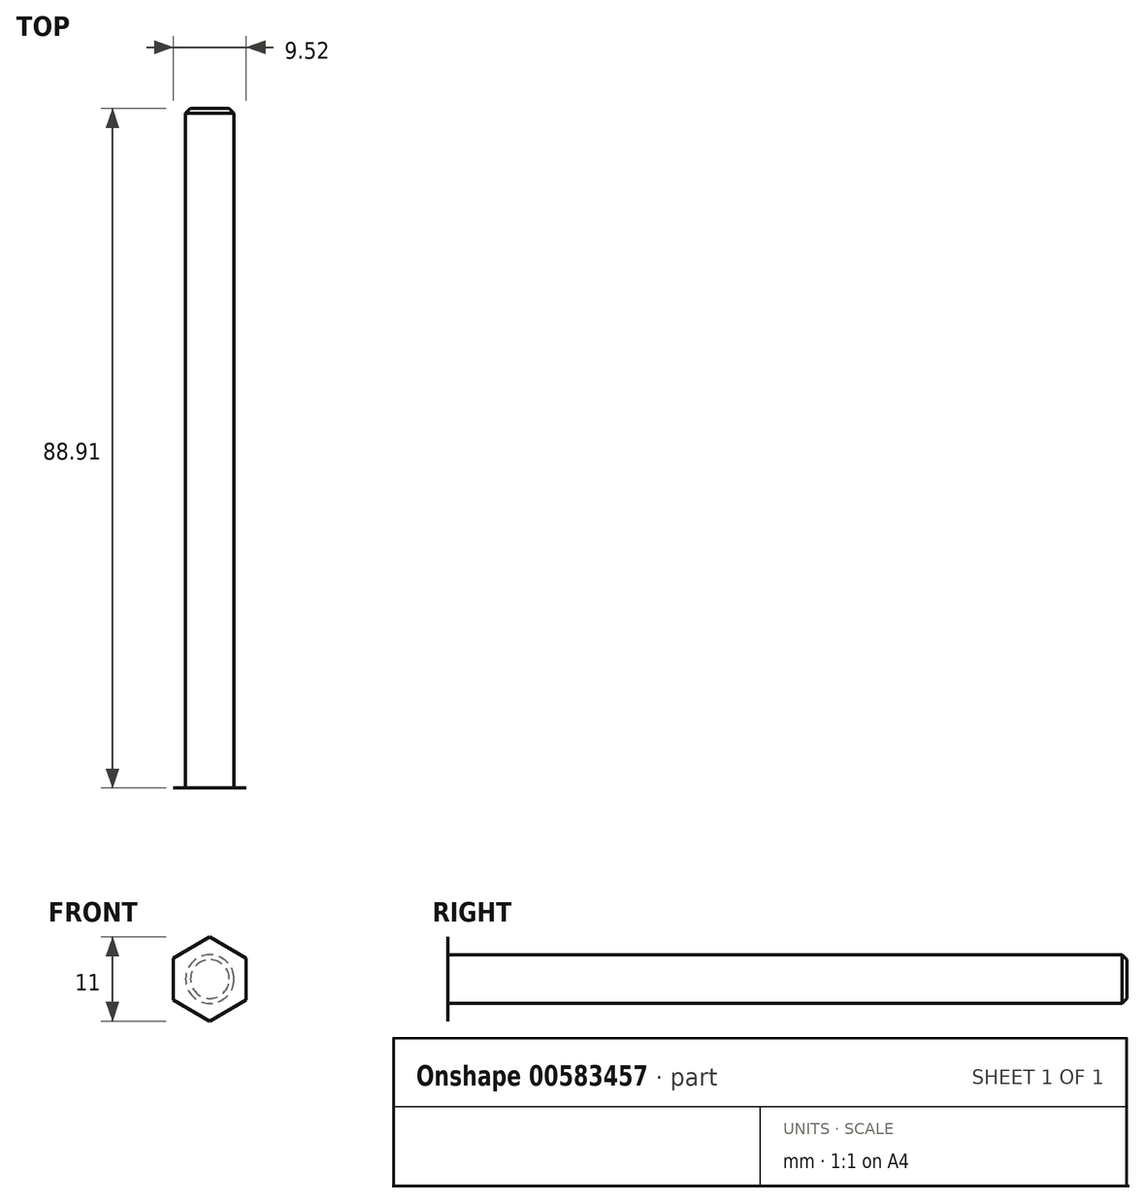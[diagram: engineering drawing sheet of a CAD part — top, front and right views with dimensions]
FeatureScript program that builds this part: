
annotation { "Feature Type Name" : "Feature", "Feature Type Description" : "" }
export const myFeature = defineFeature(function(context is Context, id is Id, definition is map)
    precondition{}
    {
        {
            assignVariable(context, id + "F0", {"name" : "BoltLen", "anyValue" : 88.9 * mm});
        }
        {
            assignVariable(context, id + "F1", {"name" : "HeadDepth", "anyValue" : 3 / 406.4 * mm});
        }
        {
            var Q0;
            Q0=qCreatedBy(makeId("Front.planeOp"),FACE);
            var sketch = newSketch(context, id + "F2", { "sketchPlane" : qUnion([Q0])});
            skCircle(sketch, "E0", {"center": v(0, 0) * mm, "radius": 3.17 * mm});
            skSolve(sketch);
        }
        {
            var Q0;
            Q0=qSketchRegion(id+"F2",true);
            extrude(context, id + "F3", {"entities" : qUnion([Q0]), "oppositeDirection" : true, "depth" : getVariable(context, 'BoltLen'), "offsetDistance" : 25.4 * mm});
        }
        {
            var Q0;
            Q0=qCreatedBy(makeId("Front.planeOp"),FACE);
            var sketch = newSketch(context, id + "F4", { "sketchPlane" : qUnion([Q0])});
            skCircle(sketch, "E1.cCircle", {"center": v(0, 0) * mm, "radius": 4.76 * mm, "construction": true});
            skLineSegment(sketch, "E1.0", {"start": v(4.76, -2.75) * mm, "end": v(0, -5.5) * mm});
            skLineSegment(sketch, "E1.1", {"start": v(0, -5.5) * mm, "end": v(-4.76, -2.75) * mm});
            skLineSegment(sketch, "E1.2", {"start": v(-4.76, -2.75) * mm, "end": v(-4.76, 2.75) * mm});
            skLineSegment(sketch, "E1.3", {"start": v(-4.76, 2.75) * mm, "end": v(0, 5.5) * mm});
            skLineSegment(sketch, "E1.4", {"start": v(0, 5.5) * mm, "end": v(4.76, 2.75) * mm});
            skLineSegment(sketch, "E1.5", {"start": v(4.76, 2.75) * mm, "end": v(4.76, -2.75) * mm});
            skPoint(sketch, "E1.0.midPoint", {"position": v(2.38, -4.12) * mm});
            skSolve(sketch);
        }
        {
            var Q0;
            Q0=qSketchRegion(id+"F4",true);
            extrude(context, id + "F5", {"entities" : qUnion([Q0]), "operationType" : NewBodyOperationType.ADD, "depth" : getVariable(context, 'HeadDepth'), "offsetDistance" : 25.4 * mm});
        }
        {
            var Q0;
            Q0=makeQuery(id+"F3.opExtrude","CAP_EDGE",EDGE,{"disambiguationData":[OSD([sQuery(id+"F2.wireOp",EDGE,"E0")])],"isStart":false});
            chamfer(context, id + "F6", {"entities" : qUnion([Q0]), "width" : 0.64 * mm, "tangentPropagation" : true});
        }
        {
            var Q0;
            Q0=qCreatedBy(makeId("Top.planeOp"),FACE);
            var sketch = newSketch(context, id + "F7", { "sketchPlane" : qUnion([Q0])});
            skLineSegment(sketch, "E2", {"start": v(11.85, -0.67) * mm, "end": v(11.85, -4.76) * mm});
            skLineSegment(sketch, "E3", {"start": v(11.85, -4.76) * mm, "end": v(4.76, -4.76) * mm});
            skLineSegment(sketch, "E4", {"start": v(4.76, -4.76) * mm, "end": v(11.85, -0.67) * mm});
            skLineSegment(sketch, "E5", {"start": v(0, 0) * mm, "end": v(0, -4.76) * mm, "construction": true});
            skSolve(sketch);
        }
        {
            var Q0;
            Q0 = qSketchRegion(id + "F7", true);
            var Q1;
            Q1=sQuery(id+"F7.wireOp",EDGE,"E5");
            revolve(context, id + "F8", {"operationType" : NewBodyOperationType.REMOVE, "entities" : qUnion([Q0]), "axis" : qUnion([Q1]), "revolveType" : RevolveType.FULL, "oppositeDirection" : true});
        }
    });
